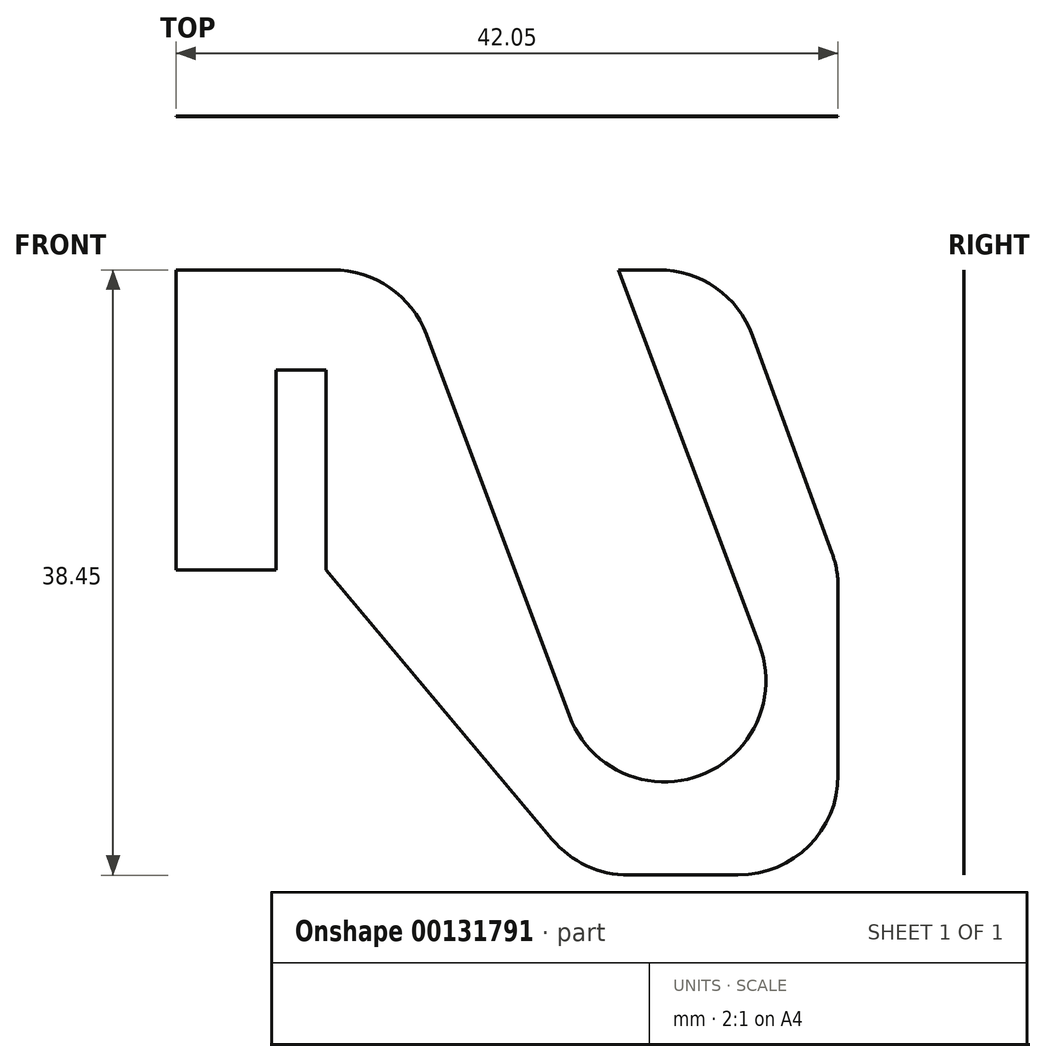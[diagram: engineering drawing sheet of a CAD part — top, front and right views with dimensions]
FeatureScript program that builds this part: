
annotation { "Feature Type Name" : "Feature", "Feature Type Description" : "" }
export const myFeature = defineFeature(function(context is Context, id is Id, definition is map)
    precondition{}
    {
        {
            var Q0;
            Q0=qCreatedBy(makeId("Front.planeOp"),FACE);
            var sketch = newSketch(context, id + "F0", { "sketchPlane" : qUnion([Q0])});
            skLineSegment(sketch, "E0", {"start": v(0, 0) * mm, "end": v(6.35, 0) * mm});
            skLineSegment(sketch, "E1", {"start": v(6.35, 0) * mm, "end": v(6.35, 12.7) * mm});
            skLineSegment(sketch, "E2", {"start": v(6.35, 12.7) * mm, "end": v(9.52, 12.7) * mm});
            skLineSegment(sketch, "E3", {"start": v(9.53, 12.7) * mm, "end": v(9.53, 0) * mm});
            skLineSegment(sketch, "E4", {"start": v(28.75, -19.4) * mm, "end": v(35.7, -19.4) * mm});
            skLineSegment(sketch, "E5", {"start": v(42.05, -13.05) * mm, "end": v(42.05, -1.13) * mm});
            skLineSegment(sketch, "E6", {"start": v(30.64, 19.05) * mm, "end": v(28.1, 19.05) * mm});
            skLineSegment(sketch, "E7", {"start": v(0, 19.05) * mm, "end": v(0, 0) * mm});
            skLineSegment(sketch, "E8", {"start": v(15.9, 14.93) * mm, "end": v(25, -9.3) * mm});
            skLineSegment(sketch, "E9", {"start": v(37.05, -4.77) * mm, "end": v(28.1, 19.05) * mm});
            skArc(sketch, "E10", {"start": v(25, -9.3) * mm, "mid": v(33.28, -13.07) * mm, "end": v(37.05, -4.77) * mm});
            skLineSegment(sketch, "E11.trimOffspring", {"start": v(9.95, 19.05) * mm, "end": v(0, 19.05) * mm});
            skPoint(sketch, "E12.visualSharp", {"position": v(14.35, 19.05) * mm});
            skArc(sketch, "E12.filletArc", {"start": v(15.9, 14.93) * mm, "mid": v(13.57, 17.92) * mm, "end": v(9.95, 19.05) * mm});
            skLineSegment(sketch, "E13", {"start": v(41.66, 1.06) * mm, "end": v(36.6, 14.88) * mm});
            skLineSegment(sketch, "E14", {"start": v(9.52, 0) * mm, "end": v(23.88, -17.13) * mm});
            skPoint(sketch, "E15.orphan", {"position": v(9.53, -19.4) * mm});
            skPoint(sketch, "E16.orphan", {"position": v(42.05, 19.05) * mm});
            skPoint(sketch, "E17.visualSharp", {"position": v(42.05, -19.4) * mm});
            skArc(sketch, "E17.filletArc", {"start": v(35.7, -19.4) * mm, "mid": v(40.2, -17.54) * mm, "end": v(42.05, -13.05) * mm});
            skPoint(sketch, "E18.visualSharp", {"position": v(25.79, -19.4) * mm});
            skArc(sketch, "E18.filletArc", {"start": v(23.88, -17.13) * mm, "mid": v(26.07, -18.8) * mm, "end": v(28.75, -19.4) * mm});
            skPoint(sketch, "E19.visualSharp", {"position": v(42.05, 0) * mm});
            skArc(sketch, "E19.filletArc", {"start": v(42.05, -1.13) * mm, "mid": v(41.95, -0.02) * mm, "end": v(41.66, 1.06) * mm});
            skPoint(sketch, "E20.visualSharp", {"position": v(35.08, 19.05) * mm});
            skArc(sketch, "E20.filletArc", {"start": v(36.6, 14.88) * mm, "mid": v(34.28, 17.9) * mm, "end": v(30.64, 19.05) * mm});
            skSolve(sketch);
        }
        {
            var Q0;
            Q0 = qSketchRegion(id + "F0", true);
            extrude(context, id + "F1", {"entities" : qUnion([Q0]), "depth" : 1 / 203.2 * mm});
        }
    });
